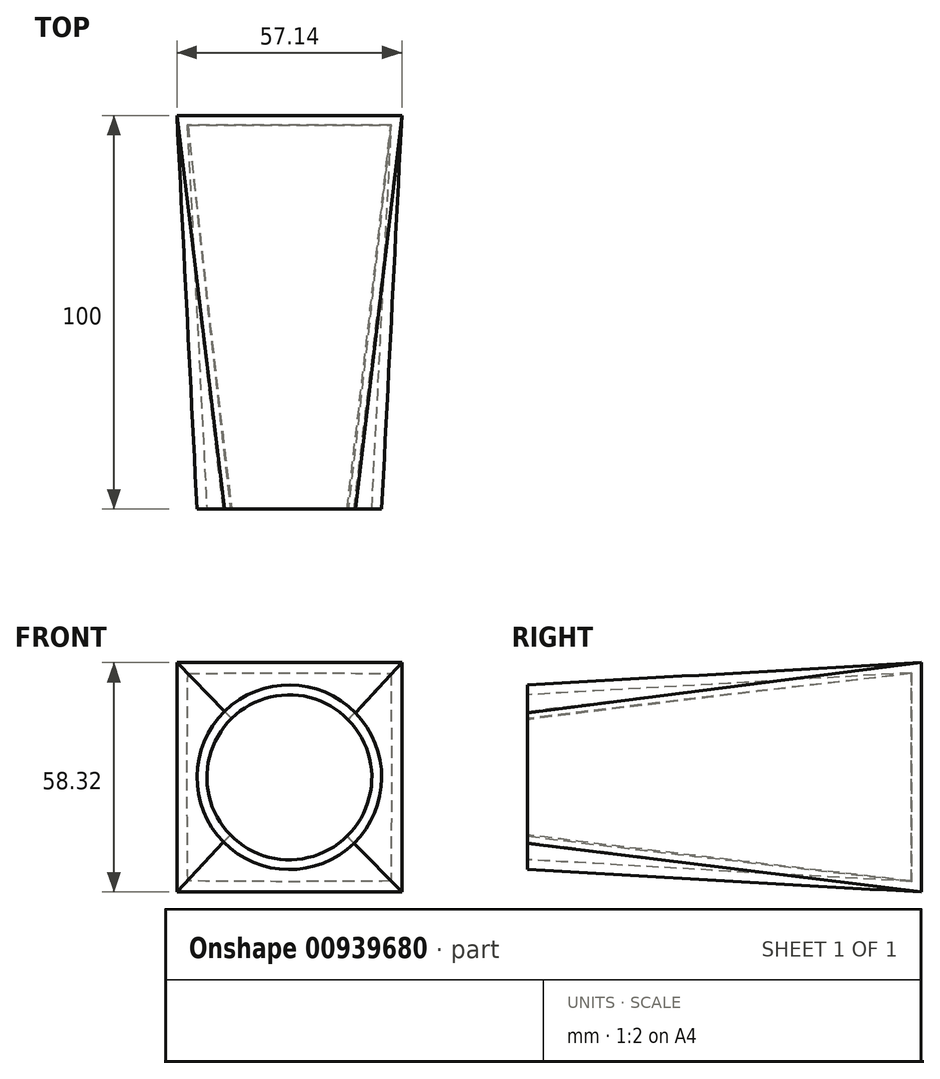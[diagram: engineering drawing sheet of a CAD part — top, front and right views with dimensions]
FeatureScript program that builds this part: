
annotation { "Feature Type Name" : "Feature", "Feature Type Description" : "" }
export const myFeature = defineFeature(function(context is Context, id is Id, definition is map)
    precondition{}
    {
        {
            var Q0;
            Q0=qCreatedBy(makeId("Front.planeOp"),FACE);
            cPlane(context, id + "F0", {"entities" : qUnion([Q0]), "cplaneType" : CPlaneType.OFFSET, "offset" : 100 * mm, "width" : 150 * mm, "height" : 150 * mm});
        }
        {
            var Q0;
            Q0=qCreatedBy(id+"F0.planeOp",FACE);
            var sketch = newSketch(context, id + "F1", { "sketchPlane" : qUnion([Q0])});
            skCircle(sketch, "E0", {"center": v(0, 0) * mm, "radius": 23.46 * mm});
            skSolve(sketch);
        }
        {
            var Q0;
            Q0=qCreatedBy(makeId("Front.planeOp"),FACE);
            var sketch = newSketch(context, id + "F2", { "sketchPlane" : qUnion([Q0])});
            skLineSegment(sketch, "E1.bottom", {"start": v(28.57, -29.16) * mm, "end": v(-28.57, -29.16) * mm});
            skLineSegment(sketch, "E1.top", {"start": v(28.57, 29.16) * mm, "end": v(-28.57, 29.16) * mm});
            skLineSegment(sketch, "E1.left", {"start": v(28.57, -29.16) * mm, "end": v(28.57, 29.16) * mm});
            skLineSegment(sketch, "E1.right", {"start": v(-28.57, -29.16) * mm, "end": v(-28.57, 29.16) * mm});
            skPoint(sketch, "E1.middle", {"position": v(0, 0) * mm});
            skSolve(sketch);
        }
        {
            var Q0;
            Q0=makeQuery(id+"F1.imprint","IMPRINT",FACE,{"disambiguationData":[TD([[makeQuery(id+"F1.imprint","IMPRINT",EDGE,{"derivedFrom":sQuery(id+"F1.wireOp",EDGE,"E0")}),1.0]])]});
            var Q1;
            Q1=makeQuery(id+"F2.imprint","IMPRINT",FACE,{"disambiguationData":[TD([[makeQuery(id+"F2.imprint","IMPRINT",EDGE,{"derivedFrom":sQuery(id+"F2.wireOp",EDGE,"E1.bottom")}),-1.0]])]});
            loft(context, id + "F3", {"sheetProfilesArray" : [{ "sheetProfileEntities" : qUnion([Q0]) }, { "sheetProfileEntities" : qUnion([Q1]) }]});
        }
        {
            var Q0;
            Q0=makeQuery(id+"F3.opLoft","CAP_FACE",FACE,{"disambiguationData":[OSD([makeQuery(id+"F1.imprint","IMPRINT",FACE,{"disambiguationData":[TD([[makeQuery(id+"F1.imprint","IMPRINT",EDGE,{"derivedFrom":sQuery(id+"F1.wireOp",EDGE,"E0")}),1.0]])]})])],"isStart":true});
            shell(context, id + "F4", {"entities" : qUnion([Q0]), "thickness" : 2.5 * mm});
        }
    });
